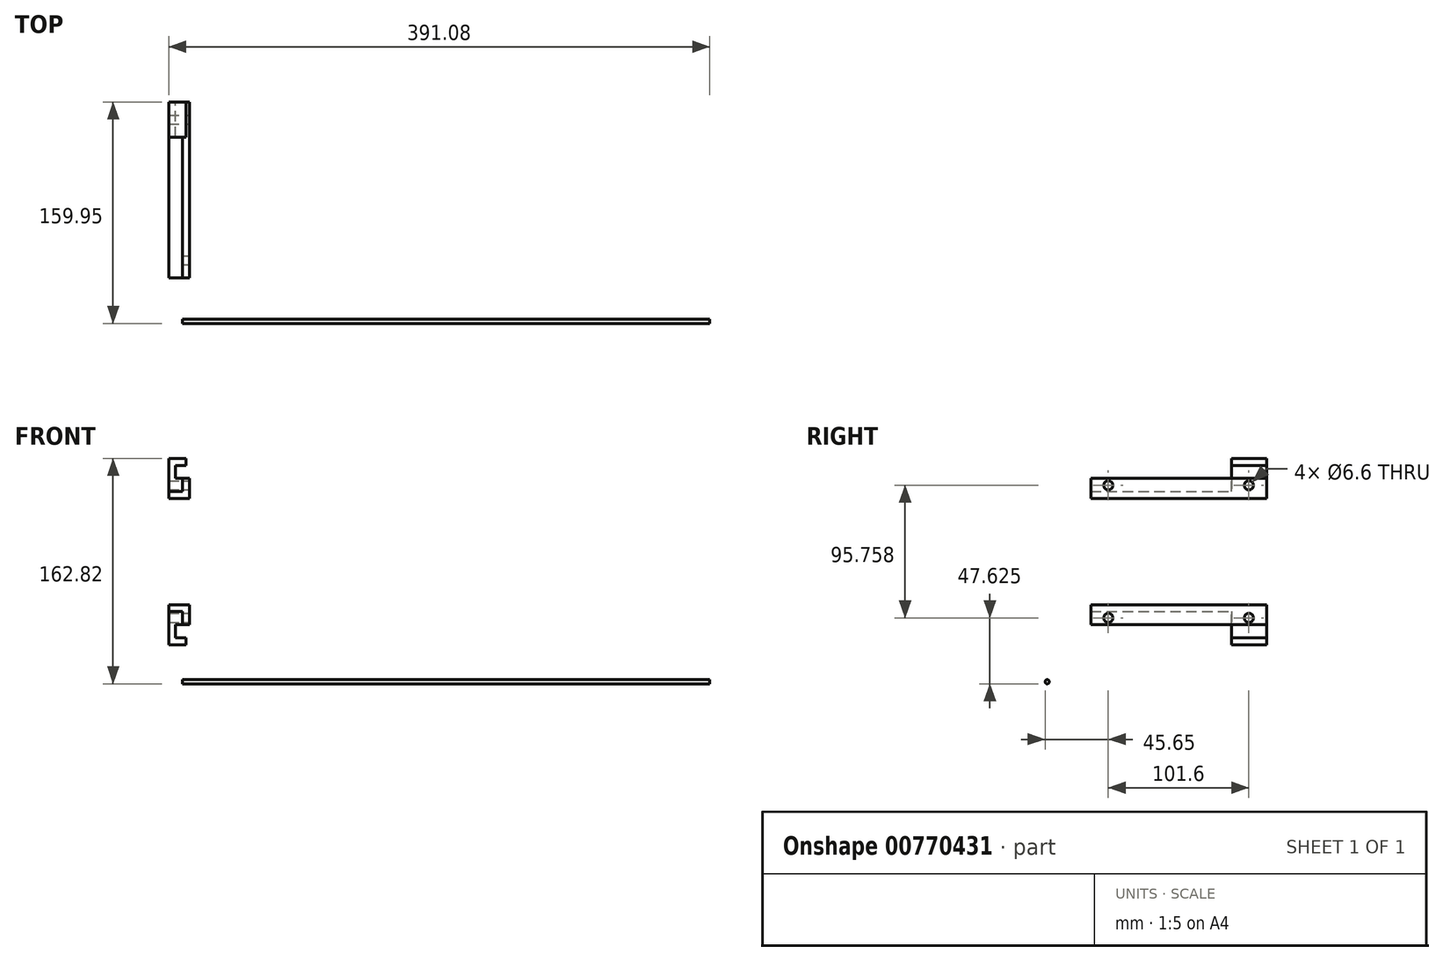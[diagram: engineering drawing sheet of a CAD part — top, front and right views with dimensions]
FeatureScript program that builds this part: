
annotation { "Feature Type Name" : "Feature", "Feature Type Description" : "" }
export const myFeature = defineFeature(function(context is Context, id is Id, definition is map)
    precondition{}
    {
        {
            var Q0;
            Q0=qCreatedBy(makeId("Front.planeOp"),FACE);
            var sketch = newSketch(context, id + "F0", { "sketchPlane" : qUnion([Q0])});
            skLineSegment(sketch, "E0.bottom", {"start": v(0, 0) * mm, "end": v(-10.08, 0) * mm});
            skLineSegment(sketch, "E0.top", {"start": v(0, -5) * mm, "end": v(-10.08, -5) * mm});
            skLineSegment(sketch, "E0.right", {"start": v(-10.08, 0) * mm, "end": v(-10.08, -5) * mm});
            skLineSegment(sketch, "E1.bottom", {"start": v(0, 0) * mm, "end": v(5, 0) * mm});
            skLineSegment(sketch, "E1.top", {"start": v(0, -14.53) * mm, "end": v(5, -14.53) * mm});
            skLineSegment(sketch, "E1.left", {"start": v(0, -5) * mm, "end": v(0, -14.53) * mm});
            skLineSegment(sketch, "E1.right", {"start": v(5, 0) * mm, "end": v(5, -14.53) * mm});
            skSolve(sketch);
        }
        {
            var Q0;
            Q0 = qSketchRegion(id + "F0", true);
            extrude(context, id + "F1", {"entities" : qUnion([Q0]), "depth" : 127 * mm, "offsetDistance" : 25.4 * mm});
        }
        {
            var Q0;
            Q0=qCreatedBy(makeId("Right.planeOp"),FACE);
            var sketch = newSketch(context, id + "F2", { "sketchPlane" : qUnion([Q0])});
            skCircle(sketch, "E2", {"center": v(-158.45, -55.65) * mm, "radius": 1.5 * mm});
            skSolve(sketch);
        }
        {
            var Q0;
            Q0 = qSketchRegion(id + "F2", true);
            extrude(context, id + "F3", {"entities" : qUnion([Q0]), "depth" : 381 * mm, "offsetDistance" : 25.4 * mm});
        }
        {
            var Q0;
            Q0=qCreatedBy(makeId("Front.planeOp"),FACE);
            cPlane(context, id + "F4", {"entities" : qUnion([Q0]), "cplaneType" : CPlaneType.OFFSET, "offset" : 12.7 * mm, "width" : 152.4 * mm, "height" : 152.4 * mm});
        }
        {
            var Q0;
            Q0=qCreatedBy(id+"F4.planeOp",FACE);
            var sketch = newSketch(context, id + "F5", { "sketchPlane" : qUnion([Q0])});
            skLineSegment(sketch, "E3.0", {"start": v(0, -5) * mm, "end": v(0, -14.53) * mm, "construction": true});
            skLineSegment(sketch, "E4.bottom", {"start": v(0, -14.53) * mm, "end": v(-5.08, -14.53) * mm});
            skLineSegment(sketch, "E4.left", {"start": v(0, -14.53) * mm, "end": v(0, -9.53) * mm});
            skLineSegment(sketch, "E5.left", {"start": v(-5.08, -14.53) * mm, "end": v(-5.08, -23.96) * mm});
            skLineSegment(sketch, "E5.right", {"start": v(-10.08, -5) * mm, "end": v(-10.08, -23.96) * mm});
            skLineSegment(sketch, "E6.bottom", {"start": v(-5.08, -23.96) * mm, "end": v(2.5, -23.96) * mm});
            skLineSegment(sketch, "E6.top", {"start": v(-10.08, -28.96) * mm, "end": v(2.5, -28.96) * mm});
            skLineSegment(sketch, "E6.left", {"start": v(-10.08, -23.96) * mm, "end": v(-10.08, -28.96) * mm});
            skLineSegment(sketch, "E6.right", {"start": v(2.5, -23.96) * mm, "end": v(2.5, -28.96) * mm});
            skPoint(sketch, "E7", {"position": v(2.5, -26.46) * mm});
            skLineSegment(sketch, "E8.0.0", {"start": v(-10.08, -5) * mm, "end": v(0, -5) * mm, "construction": true});
            skLineSegment(sketch, "E8.0.2", {"start": v(0, -14.53) * mm, "end": v(5, -14.53) * mm, "construction": true});
            skLineSegment(sketch, "E8.0.3", {"start": v(5, -14.53) * mm, "end": v(5, 0) * mm, "construction": true});
            skLineSegment(sketch, "E8.0.4", {"start": v(5, 0) * mm, "end": v(-10.08, 0) * mm, "construction": true});
            skLineSegment(sketch, "E8.0.5", {"start": v(-10.08, 0) * mm, "end": v(-10.08, -5) * mm, "construction": true});
            skPoint(sketch, "E9", {"position": v(2.5, -14.53) * mm});
            skLineSegment(sketch, "E10", {"start": v(0, -14.53) * mm, "end": v(0, -5) * mm});
            skLineSegment(sketch, "E11", {"start": v(-10.08, -5) * mm, "end": v(0, -5) * mm});
            skSolve(sketch);
        }
        {
            var Q0;
            Q0 = qSketchRegion(id + "F5", true);
            extrude(context, id + "F6", {"entities" : qUnion([Q0]), "operationType" : NewBodyOperationType.ADD, "depth" : 12.7 * mm, "offsetDistance" : 25.4 * mm, "hasSecondDirection" : true, "secondDirectionOppositeDirection" : true, "secondDirectionDepth" : 12.7 * mm});
        }
        {
            var Q0;
            Q0=makeQuery(id+"F1.opExtrude","SWEPT_FACE",FACE,{"disambiguationData":[OSD([sQuery(id+"F0.wireOp",EDGE,"E1.right")])]});
            var sketch = newSketch(context, id + "F7", { "sketchPlane" : qUnion([Q0])});
            skPoint(sketch, "E12", {"position": v(-114.3, -9.53) * mm});
            skPoint(sketch, "E13", {"position": v(-12.7, -9.53) * mm});
            skSolve(sketch);
        }
        {
            var Q0;
            Q0=sQuery(id+"F7.wireOp",VERTEX,"E12");
            var Q1;
            Q1=sQuery(id+"F7.wireOp",VERTEX,"E13");
            var Q2;
            Q2=makeQuery(id+"F1.opExtrude","SWEPT_BODY",BODY,{"disambiguationData":[OSD([sQuery(id+"F0.wireOp",EDGE,"E0.bottom"),sQuery(id+"F0.wireOp",EDGE,"E0.top"),sQuery(id+"F0.wireOp",EDGE,"E0.right"),sQuery(id+"F0.wireOp",EDGE,"E1.bottom"),sQuery(id+"F0.wireOp",EDGE,"E1.top"),sQuery(id+"F0.wireOp",EDGE,"E1.left"),sQuery(id+"F0.wireOp",EDGE,"E1.right")])]});
            hole(context, id + "F8", {"style" : HoleStyle.SIMPLE, "endStyle" : HoleEndStyle.THROUGH, "standardTappedOrClearance" : lookupTablePath({ "standard" : "ISO", "fit" : "Normal", "size" : "M6", "type" : "Clearance" }), "standardBlindInLast" : lookupTablePath({ "fit" : "Standard", "standard" : "ISO", "size" : "M6", "type" : "Clearance" }), "holeDiameter" : 6.6 * mm, "majorDiameter" : 6.35 * mm, "isTappedThrough" : true, "tappedDepth" : 12.7 * mm, "tapClearance" : 3, "locations" : qUnion([Q0, Q1]), "scope" : qUnion([Q2])});
        }
        {
            var Q0;
            Q0=makeQuery(id+"F1.opExtrude","SWEPT_BODY",BODY,{"disambiguationData":[OSD([sQuery(id+"F0.wireOp",EDGE,"E0.bottom"),sQuery(id+"F0.wireOp",EDGE,"E0.top"),sQuery(id+"F0.wireOp",EDGE,"E0.right"),sQuery(id+"F0.wireOp",EDGE,"E1.bottom"),sQuery(id+"F0.wireOp",EDGE,"E1.top"),sQuery(id+"F0.wireOp",EDGE,"E1.left"),sQuery(id+"F0.wireOp",EDGE,"E1.right")])]});
            var Q1;
            Q1=makeQuery(id+"F1.opExtrude","SWEPT_FACE",FACE,{"disambiguationData":[OSD([sQuery(id+"F0.wireOp",EDGE,"E0.bottom"),sQuery(id+"F0.wireOp",EDGE,"E1.bottom")])]});
            mirror(context, id + "F9", {"entities" : qUnion([Q0]), "mirrorPlane" : qUnion([Q1])});
        }
        {
            var Q0;
            Q0=makeQuery(id+"F9.opPattern","COPY",BODY,{"derivedFrom":makeQuery(id+"F1.opExtrude","SWEPT_BODY",BODY,{"disambiguationData":[OSD([sQuery(id+"F0.wireOp",EDGE,"E0.bottom"),sQuery(id+"F0.wireOp",EDGE,"E0.top"),sQuery(id+"F0.wireOp",EDGE,"E0.right"),sQuery(id+"F0.wireOp",EDGE,"E1.bottom"),sQuery(id+"F0.wireOp",EDGE,"E1.top"),sQuery(id+"F0.wireOp",EDGE,"E1.left"),sQuery(id+"F0.wireOp",EDGE,"E1.right")])]}),"instanceName":"1"});
            transform(context, id + "F10", {"entities" : qUnion([Q0]), "transformType" : TransformType.TRANSLATION_3D, "dx" : 0 * mm, "dy" : 0 * mm, "dz" : 76.7 * mm, "makeCopy" : false});
        }
    });
